# Revit family: Elevator_LandingDoors_Garaventa_3-Panel-Sliding
name_source: partatom
category: Doors
units: mm (PartAtom-declared; Revit-internal decimal feet)

## family parameters
Always vertical = Yes
Classification Number = 23.50.05.11.24.11
Cut with Voids When Loaded = No
Host = Wall
Room Calculation Point = No
Shared = No

## types (1)
- Residential
    Analytic Construction = <None>
    Assembly Code = D1010100
    Construction Details = http://www.arcat.com
    Description = Garaventa Lift Elvoron 3 Panel Sliding Landing Door - as Specified
    Expected Lifespan (Years) = 0
    Fire Rating = as Specified
    Frame Depth = 0' - 7 11/16"
    Function = Interior
    Green Building-LEED = http://www.arcat.com
    Jamb Width_Sides = 0' - 4"
    Keynote = 14 20 00
    Maintenance Schedule (Months) = 0
    Manufacturer = Garaventa Lift
    Manufacturer Fax = 604-594-9915
    Manufacturer Website = http://www.garaventalift.com
    Model = 3 Panel Sliding
    Product Data = http://www.arcat.com
    RO Spacing Sides = 0' - 2 3/32"
    Sales Information = http://www.garaventalift.com
    Specification = http://www.arcat.com
    Thickness = 0' - 0"
    Three Panel = Yes
    Two Panel = No
    URL = http://www.garaventalift.com
    Wall Closure = By host
    Warranty Duration (Years) = 0

## geometry (parser evidence)
native form markers: Sweep x8
no freeform markers — native parametric forms only
